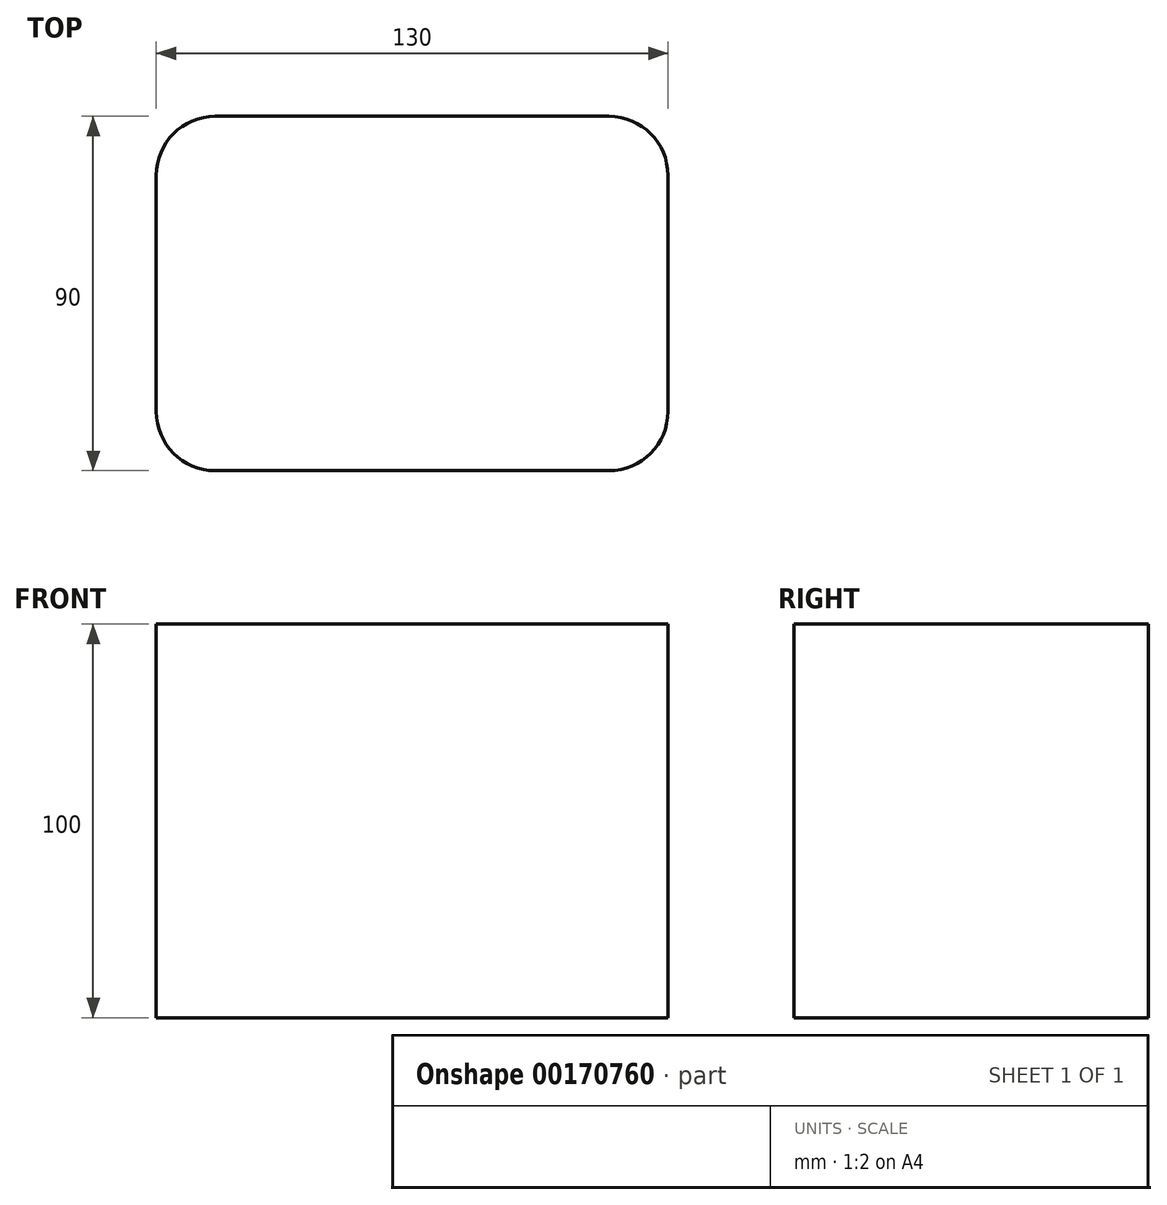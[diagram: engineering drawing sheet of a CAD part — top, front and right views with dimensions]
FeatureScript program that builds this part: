
annotation { "Feature Type Name" : "Feature", "Feature Type Description" : "" }
export const myFeature = defineFeature(function(context is Context, id is Id, definition is map)
    precondition{}
    {
        {
            var Q0;
            Q0=qCreatedBy(makeId("Top.planeOp"),FACE);
            var sketch = newSketch(context, id + "F0", { "sketchPlane" : qUnion([Q0])});
            skLineSegment(sketch, "E0.bottom", {"start": v(50, -45) * mm, "end": v(-50, -45) * mm});
            skLineSegment(sketch, "E0.top", {"start": v(50, 45) * mm, "end": v(-50, 45) * mm});
            skLineSegment(sketch, "E0.left", {"start": v(65, -30) * mm, "end": v(65, 30) * mm});
            skLineSegment(sketch, "E0.right", {"start": v(-65, -30) * mm, "end": v(-65, 30) * mm});
            skPoint(sketch, "E0.middle", {"position": v(0, 0) * mm});
            skPoint(sketch, "E1.visualSharp", {"position": v(-65, 45) * mm});
            skArc(sketch, "E1.filletArc", {"start": v(-50, 45) * mm, "mid": v(-60.6, 40.6) * mm, "end": v(-65, 30) * mm});
            skPoint(sketch, "E2.visualSharp", {"position": v(-65, -45) * mm});
            skArc(sketch, "E2.filletArc", {"start": v(-65, -30) * mm, "mid": v(-60.6, -40.6) * mm, "end": v(-50, -45) * mm});
            skPoint(sketch, "E3.visualSharp", {"position": v(65, -45) * mm});
            skArc(sketch, "E3.filletArc", {"start": v(50, -45) * mm, "mid": v(60.6, -40.6) * mm, "end": v(65, -30) * mm});
            skPoint(sketch, "E4.visualSharp", {"position": v(65, 45) * mm});
            skArc(sketch, "E4.filletArc", {"start": v(65, 30) * mm, "mid": v(60.6, 40.6) * mm, "end": v(50, 45) * mm});
            skSolve(sketch);
        }
        {
            var Q0;
            Q0 = qSketchRegion(id + "F0", true);
            extrude(context, id + "F1", {"entities" : qUnion([Q0]), "depth" : 100 * mm});
        }
    });
